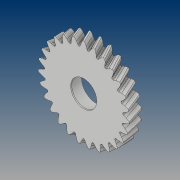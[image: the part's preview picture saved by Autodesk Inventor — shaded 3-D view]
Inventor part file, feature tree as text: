
AUTODESK INVENTOR PART (.ipt)
format: ipt  version: 2021 (Build 250183000, 183)  size: 909,824 bytes
history: native  units: mm
features: thread x4, sketch x4, extrude x2, revolve x2, pattern_circular x2, plane x1
ambient origin geometry x8: Origin, YZ Plane, XZ Plane, XY Plane, X Axis, Y Axis, Z Axis, Center Point
bodies: Solid2 (feature_tree), Solid1 (feature_tree)
feature tree (15):
  extrude  "Extrusion1"  Depth=10.0mm TaperAngle=0.0deg
  revolve  "Revolution1"  [1 undecoded]
  extrude  "Extrusion2"  Depth=10.0mm
  pattern_circular  "Circular Pattern1"  Count=3  [1 undecoded]
  thread  "Thread1"  [1 undecoded]
  thread  "Thread2"  [1 undecoded]
  thread  "Thread3"  [1 undecoded]
  thread  "Thread4"  [1 undecoded]
  plane  "Work Plane1"
  revolve  "Revolution2"  [1 undecoded]
  pattern_circular  "Circular Pattern2"  [2 undecoded]
  sketch  "Sketch1"  dims[d0=52.0mm d1=10.0mm d2=0.0mm]
  sketch  "Sketch2"  dims[d3=9.0mm d4=3.0mm]
  sketch  "Sketch3"  dims[d5=90.0deg d6=4.0mm d7=30.0mm d8=8.0mm d9=0.0mm d10=40.0mm d11=360.0deg d13=10.0mm d14=0.0mm d15=10.0mm d16=0.0mm]
  sketch  "Sketch4"  dims[d17=10.0mm d18=0.0mm d19=10.0mm d20=0.0mm d21=22.0mm d22=135.0deg d23=45.0deg d24=90.0deg d25=40.0mm d26=360.0deg]
note: 9 required parameter values undecoded (feature->parameter linkage not recoverable at this tier; creation-order binding heuristic only, values carry confidence <= 0.55)